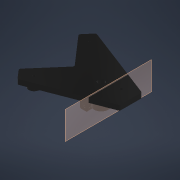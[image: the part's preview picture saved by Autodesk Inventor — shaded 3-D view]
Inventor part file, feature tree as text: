
AUTODESK INVENTOR PART (.ipt)
format: ipt  version: 2021 (Build 250183000, 183)  size: 323,072 bytes
history: native  units: mm
features: extrude x7, other x5, fillet x5, projected_geometry x2, plane x1
ambient origin geometry x8: Origin, YZ Plane, XZ Plane, XY Plane, X Axis, Y Axis, Z Axis, Center Point
bodies: Solid1 (feature_tree)
feature tree (20):
  other  "referencce"
  other  "shape"
  other  "shape_fillets"
  extrude  "base_shape"  Depth=14.0mm
  extrude  "main_mount"  Depth=14.0mm
  extrude  "main_mount_ext_through"  Depth=14.0mm
  fillet  "main_mount_fillet"  Radius=28.0mm
  extrude  "rod_support"  Depth=8.0mm
  fillet  "rod_support_fillet"  Radius=6.0mm
  extrude  "arm_holder"  Depth=5.0mm
  fillet  "rod_holder_to_arm_holder1"  Radius=19.373155mm
  fillet  "rod_holder_to_arm_holder2"  Radius=19.373155mm
  extrude  "arm_hole"  Depth=100.0mm
  fillet  "arm_holder_top"  Radius=100.0mm
  plane  "Work Plane1"
  extrude  "rod_screw"  Depth=10.0mm
  other  "arm_hole_sketch"
  other  "rod_screw_sketch"
  projected_geometry  "Projected Loop1"
  projected_geometry  "Projected Loop2"
